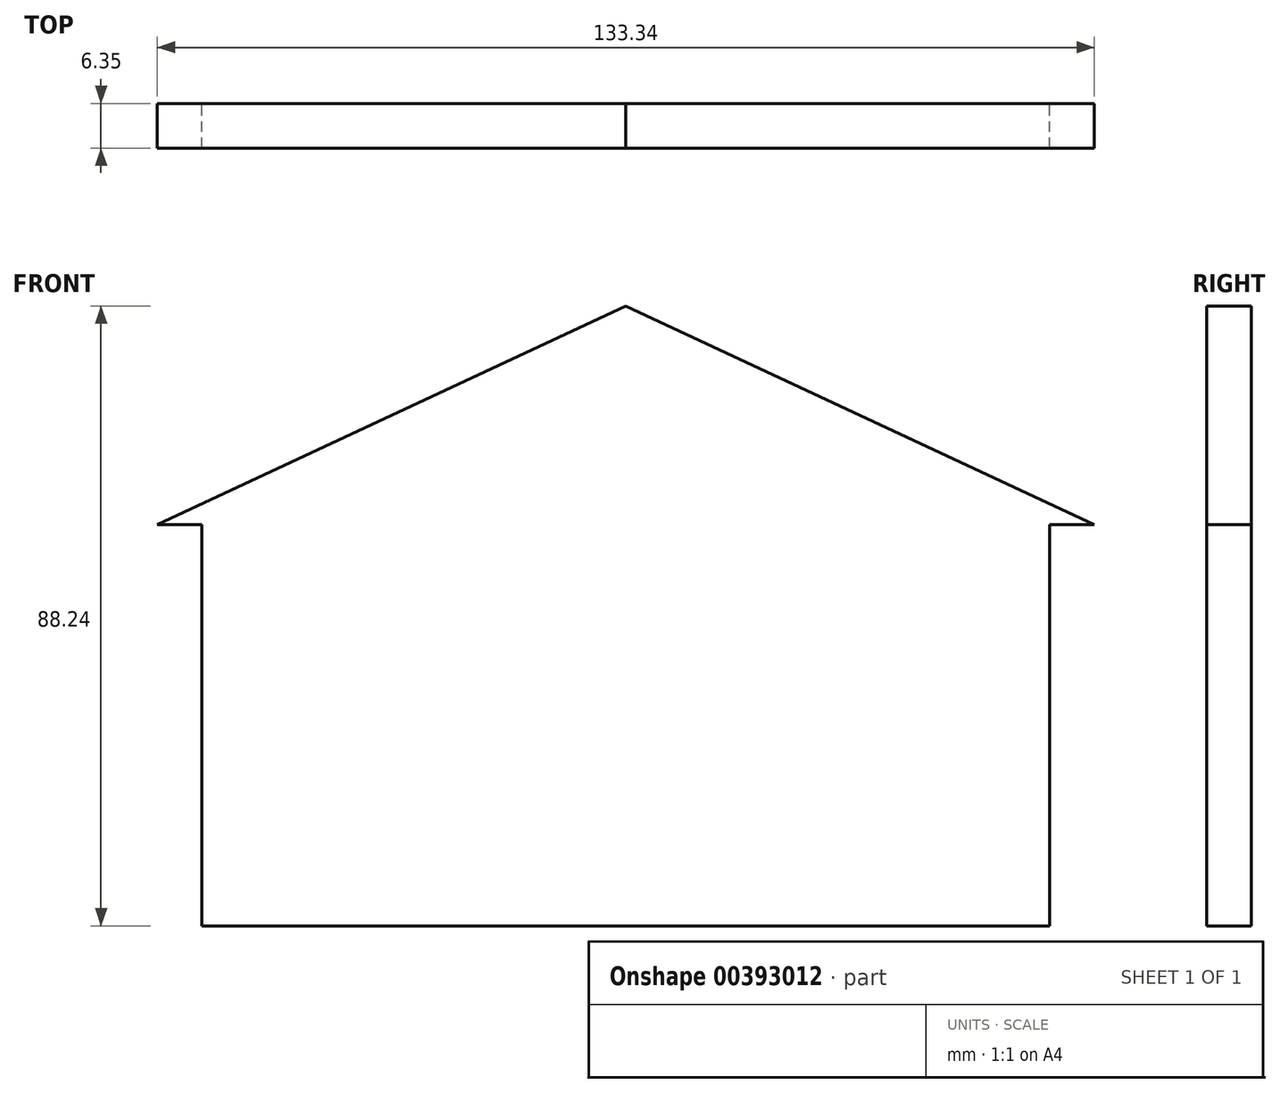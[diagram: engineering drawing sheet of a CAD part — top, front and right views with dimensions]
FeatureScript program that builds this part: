
annotation { "Feature Type Name" : "Feature", "Feature Type Description" : "" }
export const myFeature = defineFeature(function(context is Context, id is Id, definition is map)
    precondition{}
    {
        {
            var Q0;
            Q0=qCreatedBy(makeId("Front.planeOp"),FACE);
            var sketch = newSketch(context, id + "F0", { "sketchPlane" : qUnion([Q0])});
            skLineSegment(sketch, "E0.bottom", {"start": v(60.33, -28.58) * mm, "end": v(-60.33, -28.58) * mm});
            skLineSegment(sketch, "E0.left", {"start": v(60.33, -28.58) * mm, "end": v(60.33, 28.58) * mm});
            skLineSegment(sketch, "E0.right", {"start": v(-60.33, -28.58) * mm, "end": v(-60.33, 28.58) * mm});
            skPoint(sketch, "E0.middle", {"position": v(0, 0) * mm});
            skLineSegment(sketch, "E1", {"start": v(-60.33, 28.58) * mm, "end": v(-66.68, 28.58) * mm});
            skLineSegment(sketch, "E2", {"start": v(60.33, 28.58) * mm, "end": v(66.67, 28.58) * mm});
            skLineSegment(sketch, "E3", {"start": v(0, -28.58) * mm, "end": v(0, 59.67) * mm, "construction": true});
            skLineSegment(sketch, "E4", {"start": v(-66.68, 28.58) * mm, "end": v(0, 59.67) * mm});
            skLineSegment(sketch, "E5", {"start": v(0, 59.67) * mm, "end": v(66.67, 28.58) * mm});
            skSolve(sketch);
        }
        {
            var Q0;
            Q0 = qSketchRegion(id + "F0", true);
            var Q1;
            Q1=makeQuery(id+"F0.imprint","IMPRINT",FACE,{"disambiguationData":[TD([[makeQuery(id+"F0.imprint","IMPRINT",EDGE,{"derivedFrom":sQuery(id+"F0.wireOp",EDGE,"E0.bottom")}),-1.0]])]});
            extrude(context, id + "F1", {"entities" : qUnion([Q0, Q1]), "depth" : 6.35 * mm});
        }
    });
